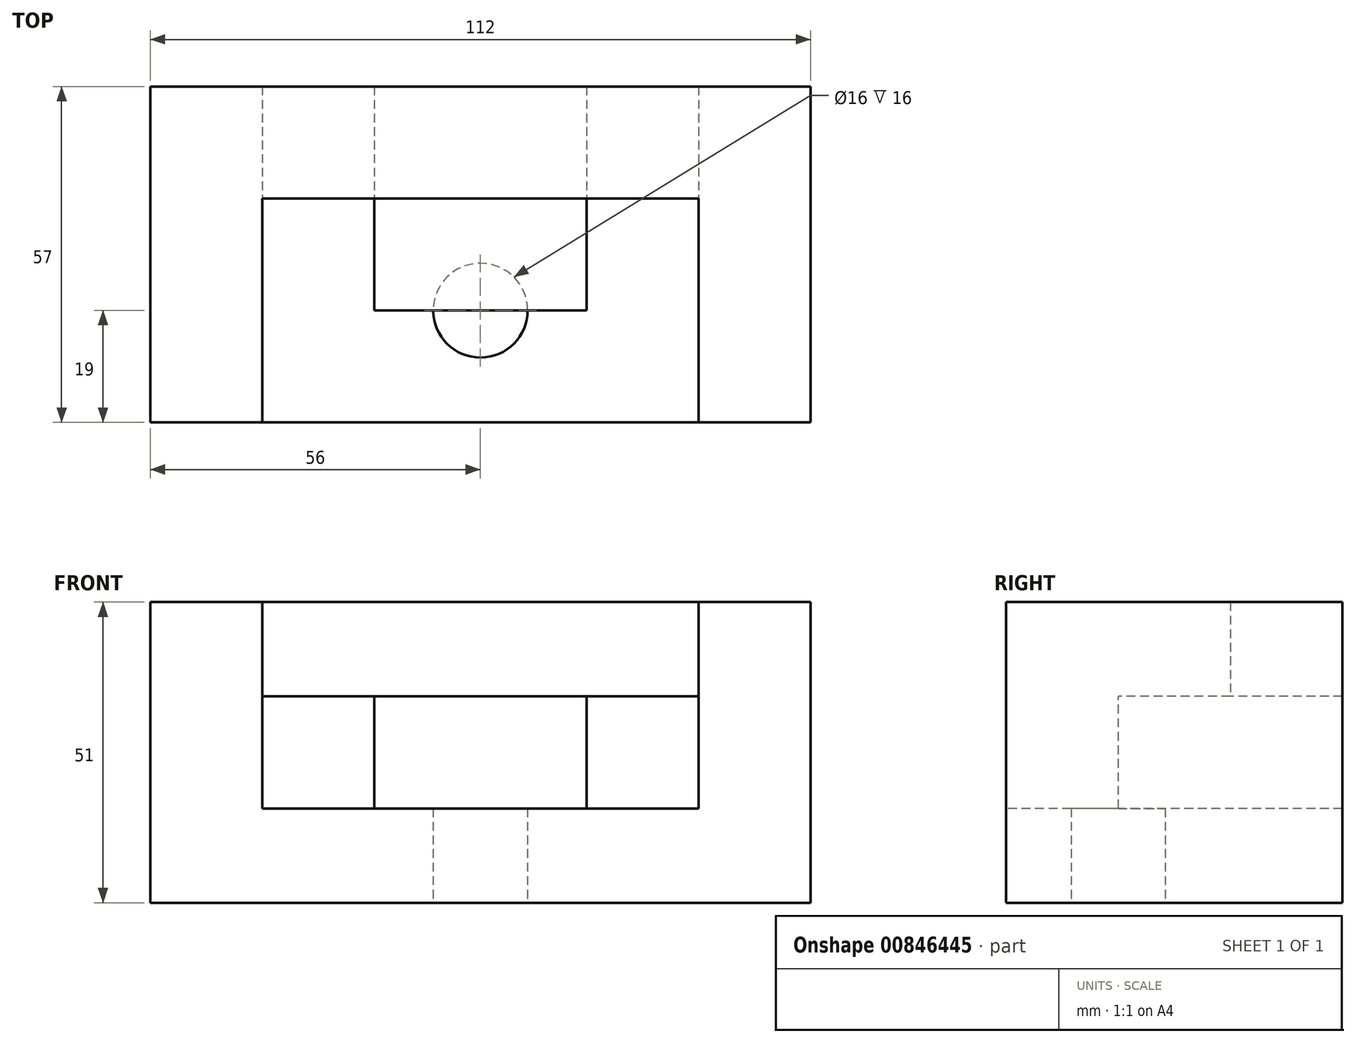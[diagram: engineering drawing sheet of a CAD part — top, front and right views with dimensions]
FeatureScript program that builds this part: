
annotation { "Feature Type Name" : "Feature", "Feature Type Description" : "" }
export const myFeature = defineFeature(function(context is Context, id is Id, definition is map)
    precondition{}
    {
        {
            var Q0;
            Q0=qCreatedBy(makeId("Front.planeOp"),FACE);
            var sketch = newSketch(context, id + "F0", { "sketchPlane" : qUnion([Q0])});
            skLineSegment(sketch, "E0.bottom", {"start": v(0, 0) * mm, "end": v(112, 0) * mm});
            skLineSegment(sketch, "E0.top", {"start": v(0, 51) * mm, "end": v(112, 51) * mm});
            skLineSegment(sketch, "E0.left", {"start": v(0, 0) * mm, "end": v(0, 51) * mm});
            skLineSegment(sketch, "E0.right", {"start": v(112, 0) * mm, "end": v(112, 51) * mm});
            skSolve(sketch);
        }
        {
            var Q0;
            Q0=makeQuery(id+"F0.imprint","IMPRINT",FACE,{"disambiguationData":[TD([[makeQuery(id+"F0.imprint","IMPRINT",EDGE,{"derivedFrom":sQuery(id+"F0.wireOp",EDGE,"E0.bottom")}),1.0]])]});
            extrude(context, id + "F1", {"entities" : qUnion([Q0]), "depth" : 57 * mm, "offsetDistance" : 25.4 * mm});
        }
        {
            var Q0;
            Q0=makeQuery(id+"F1.opExtrude","CAP_FACE",FACE,{"disambiguationData":[OSD([sQuery(id+"F0.wireOp",EDGE,"E0.bottom"),sQuery(id+"F0.wireOp",EDGE,"E0.top"),sQuery(id+"F0.wireOp",EDGE,"E0.left"),sQuery(id+"F0.wireOp",EDGE,"E0.right")])],"isStart":false});
            var sketch = newSketch(context, id + "F2", { "sketchPlane" : qUnion([Q0])});
            skLineSegment(sketch, "E1", {"start": v(0, 51) * mm, "end": v(19, 51) * mm});
            skLineSegment(sketch, "E2", {"start": v(19, 51) * mm, "end": v(19, 35) * mm});
            skLineSegment(sketch, "E3", {"start": v(19, 35) * mm, "end": v(93, 35) * mm});
            skLineSegment(sketch, "E4", {"start": v(93, 35) * mm, "end": v(93, 51) * mm});
            skLineSegment(sketch, "E5", {"start": v(93, 51) * mm, "end": v(112, 51) * mm});
            skLineSegment(sketch, "E6", {"start": v(19, 51) * mm, "end": v(93, 51) * mm});
            skSolve(sketch);
        }
        {
            var Q0;
            Q0=makeQuery(id+"F2.imprint","IMPRINT",FACE,{"disambiguationData":[TD([[makeQuery(id+"F2.imprint","IMPRINT",EDGE,{"derivedFrom":sQuery(id+"F2.wireOp",EDGE,"E2")}),1.0]])]});
            extrude(context, id + "F3", {"entities" : qUnion([Q0]), "operationType" : NewBodyOperationType.REMOVE, "oppositeDirection" : true, "depth" : 38 * mm, "offsetDistance" : 25.4 * mm});
        }
        {
            var Q0;
            Q0=makeQuery(id+"F1.opExtrude","CAP_FACE",FACE,{"disambiguationData":[OSD([sQuery(id+"F0.wireOp",EDGE,"E0.bottom"),sQuery(id+"F0.wireOp",EDGE,"E0.top"),sQuery(id+"F0.wireOp",EDGE,"E0.left"),sQuery(id+"F0.wireOp",EDGE,"E0.right")])],"isStart":false});
            var sketch = newSketch(context, id + "F4", { "sketchPlane" : qUnion([Q0])});
            skLineSegment(sketch, "E7", {"start": v(19, 35) * mm, "end": v(19, 16) * mm});
            skLineSegment(sketch, "E8", {"start": v(19, 16) * mm, "end": v(93, 16) * mm});
            skLineSegment(sketch, "E9", {"start": v(93, 16) * mm, "end": v(93, 35) * mm});
            skLineSegment(sketch, "E10", {"start": v(19, 35) * mm, "end": v(38, 35) * mm});
            skLineSegment(sketch, "E11", {"start": v(38, 35) * mm, "end": v(38, 16) * mm});
            skLineSegment(sketch, "E12", {"start": v(38, 16) * mm, "end": v(74, 16) * mm});
            skLineSegment(sketch, "E13", {"start": v(74, 16) * mm, "end": v(74, 35) * mm});
            skLineSegment(sketch, "E14", {"start": v(74, 35) * mm, "end": v(93, 35) * mm});
            skSolve(sketch);
        }
        {
            var Q0;
            {var subQ0=sQuery(id+"F4.wireOp",EDGE,"E7");Q0=makeQuery(id+"F4.imprint","IMPRINT",FACE,{"disambiguationData":[TD([[makeQuery(id+"F4.imprint","IMPRINT",EDGE,{"derivedFrom":subQ0}),1.0]])]});}
            var Q1;
            {var subQ0=sQuery(id+"F4.wireOp",EDGE,"E9");Q1=makeQuery(id+"F4.imprint","IMPRINT",FACE,{"disambiguationData":[TD([[makeQuery(id+"F4.imprint","IMPRINT",EDGE,{"derivedFrom":subQ0}),1.0]])]});}
            extrude(context, id + "F5", {"entities" : qUnion([Q0, Q1]), "operationType" : NewBodyOperationType.REMOVE, "endBound" : BoundingType.THROUGH_ALL, "oppositeDirection" : true, "depth" : 25.4 * mm, "offsetDistance" : 25.4 * mm});
        }
        {
            var Q0;
            Q0=makeQuery(id+"F1.opExtrude","CAP_FACE",FACE,{"disambiguationData":[OSD([sQuery(id+"F0.wireOp",EDGE,"E0.bottom"),sQuery(id+"F0.wireOp",EDGE,"E0.top"),sQuery(id+"F0.wireOp",EDGE,"E0.left"),sQuery(id+"F0.wireOp",EDGE,"E0.right")])],"isStart":false});
            var sketch = newSketch(context, id + "F6", { "sketchPlane" : qUnion([Q0])});
            skLineSegment(sketch, "E15", {"start": v(38, 16) * mm, "end": v(74, 16) * mm});
            skLineSegment(sketch, "E16", {"start": v(74, 16) * mm, "end": v(74, 35) * mm});
            skLineSegment(sketch, "E17", {"start": v(74, 35) * mm, "end": v(38, 35) * mm});
            skLineSegment(sketch, "E18", {"start": v(38, 35) * mm, "end": v(38, 16) * mm});
            skSolve(sketch);
        }
        {
            var Q0;
            Q0 = qSketchRegion(id + "F6", true);
            extrude(context, id + "F7", {"entities" : qUnion([Q0]), "operationType" : NewBodyOperationType.REMOVE, "oppositeDirection" : true, "depth" : 19 * mm, "offsetDistance" : 25.4 * mm});
        }
        {
            var Q0;
            Q0=makeQuery(id+"F1.opExtrude","SWEPT_FACE",FACE,{"disambiguationData":[OSD([sQuery(id+"F0.wireOp",EDGE,"E0.bottom")])]});
            var sketch = newSketch(context, id + "F8", { "sketchPlane" : qUnion([Q0])});
            skLineSegment(sketch, "E19", {"start": v(112, 57) * mm, "end": v(56, 57) * mm});
            skLineSegment(sketch, "E20", {"start": v(56, 57) * mm, "end": v(56, 38) * mm});
            skCircle(sketch, "E21", {"center": v(56, 38) * mm, "radius": 8 * mm});
            skSolve(sketch);
        }
        {
            var Q0;
            Q0=makeQuery(id+"F8.imprint","IMPRINT",FACE,{"disambiguationData":[TD([[makeQuery(id+"F8.imprint","IMPRINT",EDGE,{"derivedFrom":sQuery(id+"F8.wireOp",EDGE,"E21")}),1.0]])]});
            extrude(context, id + "F9", {"entities" : qUnion([Q0]), "operationType" : NewBodyOperationType.REMOVE, "oppositeDirection" : true, "depth" : 16 * mm, "offsetDistance" : 25.4 * mm});
        }
    });
